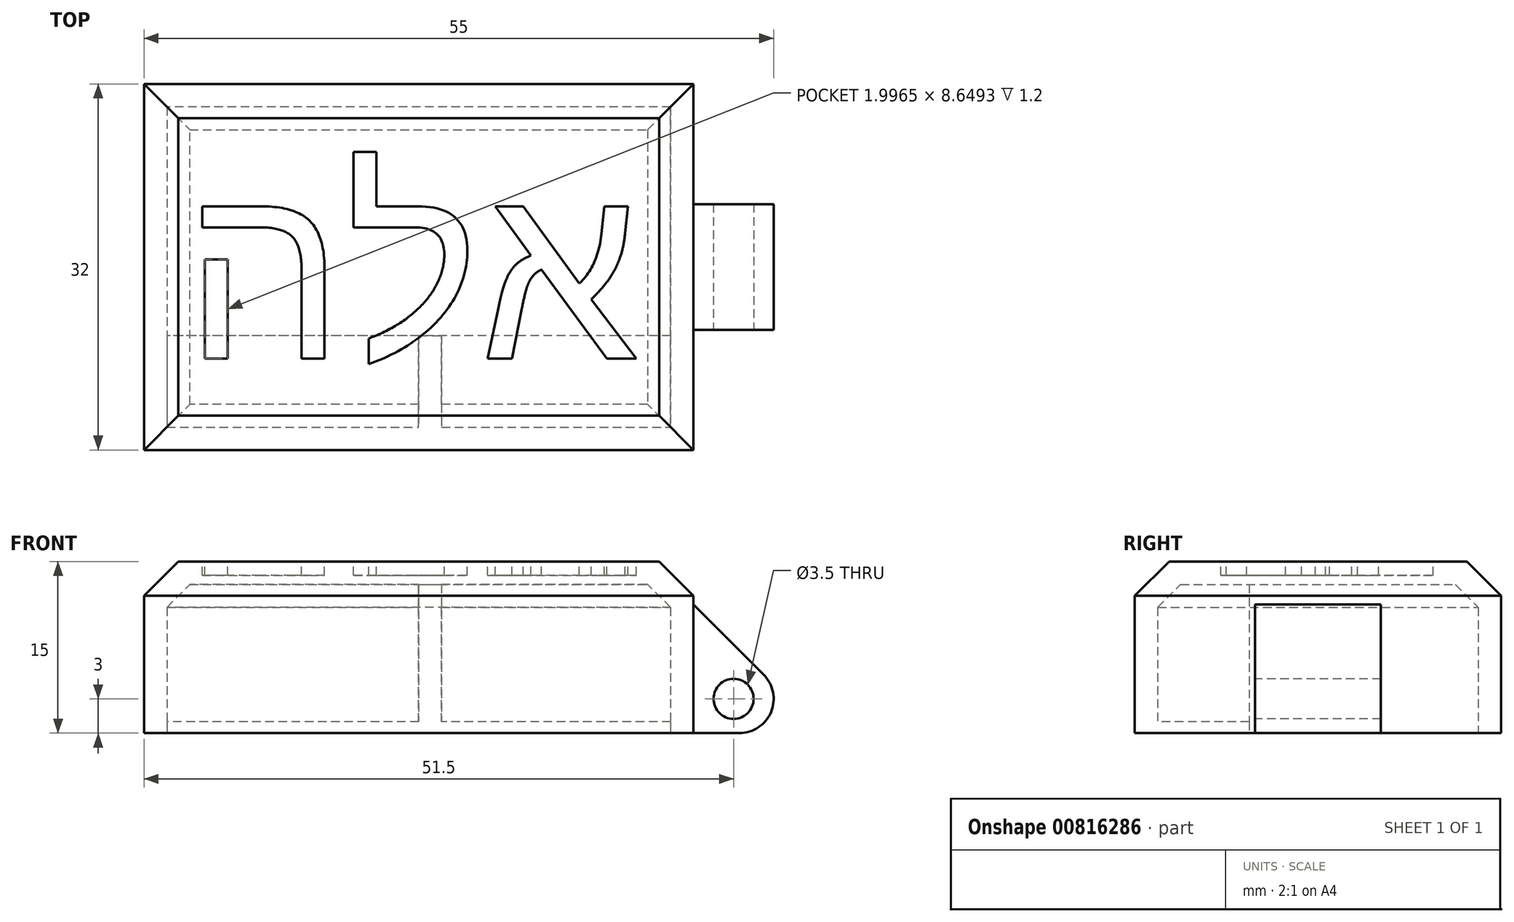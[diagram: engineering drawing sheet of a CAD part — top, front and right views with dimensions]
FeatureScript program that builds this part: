
annotation { "Feature Type Name" : "Feature", "Feature Type Description" : "" }
export const myFeature = defineFeature(function(context is Context, id is Id, definition is map)
    precondition{}
    {
        {
            var Q0;
            Q0=qCreatedBy(makeId("Top.planeOp"),FACE);
            var sketch = newSketch(context, id + "F0", { "sketchPlane" : qUnion([Q0])});
            skLineSegment(sketch, "E0.bottom", {"start": v(0, 0) * mm, "end": v(48, 0) * mm});
            skLineSegment(sketch, "E0.top", {"start": v(0, 32) * mm, "end": v(48, 32) * mm});
            skLineSegment(sketch, "E0.left", {"start": v(0, 0) * mm, "end": v(0, 32) * mm});
            skLineSegment(sketch, "E0.right", {"start": v(48, 0) * mm, "end": v(48, 32) * mm});
            skSolve(sketch);
        }
        {
            var Q0;
            Q0=makeQuery(id+"F0.imprint","IMPRINT",FACE,{"disambiguationData":[TD([[makeQuery(id+"F0.imprint","IMPRINT",EDGE,{"derivedFrom":sQuery(id+"F0.wireOp",EDGE,"E0.bottom")}),1.0]])]});
            extrude(context, id + "F1", {"entities" : qUnion([Q0]), "depth" : 15 * mm, "offsetDistance" : 25 * mm});
        }
        {
            var Q0;
            Q0=makeQuery(id+"F1.opExtrude","CAP_FACE",FACE,{"disambiguationData":[OSD([sQuery(id+"F0.wireOp",EDGE,"E0.bottom"),sQuery(id+"F0.wireOp",EDGE,"E0.top"),sQuery(id+"F0.wireOp",EDGE,"E0.left"),sQuery(id+"F0.wireOp",EDGE,"E0.right")])],"isStart":true});
            var sketch = newSketch(context, id + "F2", { "sketchPlane" : qUnion([Q0])});
            skLineSegment(sketch, "E1.bottom", {"start": v(46, -30) * mm, "end": v(2, -30) * mm});
            skLineSegment(sketch, "E1.top", {"start": v(46, -2) * mm, "end": v(2, -2) * mm});
            skLineSegment(sketch, "E1.left", {"start": v(46, -30) * mm, "end": v(46, -2) * mm});
            skLineSegment(sketch, "E1.right", {"start": v(2, -30) * mm, "end": v(2, -2) * mm});
            skSolve(sketch);
        }
        {
            var Q0;
            Q0=qSketchRegion(id+"F2",true);
            extrude(context, id + "F3", {"entities" : qUnion([Q0]), "operationType" : NewBodyOperationType.REMOVE, "oppositeDirection" : true, "depth" : 13 * mm, "offsetDistance" : 25 * mm});
        }
        {
            var Q0;
            Q0=makeQuery(id+"F1.opExtrude","CAP_FACE",FACE,{"disambiguationData":[OSD([sQuery(id+"F0.wireOp",EDGE,"E0.bottom"),sQuery(id+"F0.wireOp",EDGE,"E0.top"),sQuery(id+"F0.wireOp",EDGE,"E0.left"),sQuery(id+"F0.wireOp",EDGE,"E0.right")])],"isStart":true});
            var sketch = newSketch(context, id + "F4", { "sketchPlane" : qUnion([Q0])});
            skLineSegment(sketch, "E2.bottom", {"start": v(48, -10.5) * mm, "end": v(55, -10.5) * mm});
            skLineSegment(sketch, "E2.top", {"start": v(48, -21.5) * mm, "end": v(55, -21.5) * mm});
            skLineSegment(sketch, "E2.left", {"start": v(48, -10.5) * mm, "end": v(48, -21.5) * mm});
            skLineSegment(sketch, "E2.right", {"start": v(55, -10.5) * mm, "end": v(55, -21.5) * mm});
            skSolve(sketch);
        }
        {
            var Q0;
            Q0=makeQuery(id+"F4.imprint","IMPRINT",FACE,{"disambiguationData":[TD([[makeQuery(id+"F4.imprint","IMPRINT",EDGE,{"derivedFrom":sQuery(id+"F4.wireOp",EDGE,"E2.bottom")}),-1.0]])]});
            var Q1;
            Q1=makeQuery(id+"F4.imprint","IMPRINT",FACE,{"disambiguationData":[TD([[makeQuery(id+"F4.imprint","IMPRINT",EDGE,{"derivedFrom":sQuery(id+"F4.wireOp",EDGE,"Fs3PQJWO-v5HL-7R1I-baSF-Dp8QI7Y0G9z7.bottom")}),-1.0]])]});
            extrude(context, id + "F5", {"entities" : qUnion([Q0, Q1]), "operationType" : NewBodyOperationType.ADD, "oppositeDirection" : true, "depth" : 6 * mm, "offsetDistance" : 25 * mm});
        }
        {
            var Q0;
            Q0=makeQuery(id+"F5.opExtrude","SWEPT_FACE",FACE,{"disambiguationData":[OSD([sQuery(id+"F4.wireOp",EDGE,"E2.bottom")])]});
            var sketch = newSketch(context, id + "F6", { "sketchPlane" : qUnion([Q0])});
            skLineSegment(sketch, "E3", {"start": v(48, 6) * mm, "end": v(55, 0) * mm, "construction": true});
            skCircle(sketch, "E4", {"center": v(51.5, 3) * mm, "radius": 1.75 * mm});
            skSolve(sketch);
        }
        {
            var Q0;
            Q0=makeQuery(id+"F6.imprint","IMPRINT",FACE,{"disambiguationData":[TD([[makeQuery(id+"F6.imprint","IMPRINT",EDGE,{"derivedFrom":sQuery(id+"F6.wireOp",EDGE,"E4")}),1.0]])]});
            extrude(context, id + "F7", {"entities" : qUnion([Q0]), "operationType" : NewBodyOperationType.REMOVE, "oppositeDirection" : true, "depth" : 60.8 * mm, "offsetDistance" : 25 * mm});
        }
        {
            var Q0;
            Q0=makeQuery(id+"F5.opExtrude","CAP_EDGE",EDGE,{"disambiguationData":[OSD([sQuery(id+"F4.wireOp",EDGE,"E2.right")])],"isStart":true});
            var Q1;
            Q1=makeQuery(id+"F5.opExtrude","CAP_EDGE",EDGE,{"disambiguationData":[OSD([sQuery(id+"F4.wireOp",EDGE,"E2.right")])],"isStart":false});
            var Q2;
            Q2=makeQuery(id+"F5.opExtrude","CAP_EDGE",EDGE,{"disambiguationData":[OSD([sQuery(id+"F4.wireOp",EDGE,"Fs3PQJWO-v5HL-7R1I-baSF-Dp8QI7Y0G9z7.right")])],"isStart":false});
            var Q3;
            Q3=makeQuery(id+"F5.opExtrude","CAP_EDGE",EDGE,{"disambiguationData":[OSD([sQuery(id+"F4.wireOp",EDGE,"Fs3PQJWO-v5HL-7R1I-baSF-Dp8QI7Y0G9z7.right")])],"isStart":true});
            fillet(context, id + "F8", {"entities" : qUnion([Q0, Q1, Q2, Q3]), "tangentPropagation" : true, "radius" : 3 * mm, "defaultsChanged" : false, "vertexSettings" : [], "allowEdgeOverflow" : false});
        }
        {
            var Q0;
            Q0=makeQuery(id+"FWko5dZgeJsUJI3_1.boolean.opBoolean","MERGE",FACE,{"derivedFrom":[makeQuery(id+"F5.boolean.opBoolean","MERGE",FACE,{"derivedFrom":[makeQuery(id+"F1.opExtrude","CAP_FACE",FACE,{"disambiguationData":[OSD([sQuery(id+"F0.wireOp",EDGE,"E0.bottom"),sQuery(id+"F0.wireOp",EDGE,"E0.top"),sQuery(id+"F0.wireOp",EDGE,"E0.left"),sQuery(id+"F0.wireOp",EDGE,"E0.right")])],"isStart":true}),makeQuery(id+"F5.opExtrude","CAP_FACE",FACE,{"disambiguationData":[OSD([sQuery(id+"F4.wireOp",EDGE,"E2.bottom"),sQuery(id+"F4.wireOp",EDGE,"E2.top"),sQuery(id+"F4.wireOp",EDGE,"E2.left"),sQuery(id+"F4.wireOp",EDGE,"E2.right")])],"isStart":true}),makeQuery(id+"F5.opExtrude","CAP_FACE",FACE,{"disambiguationData":[OSD([sQuery(id+"F4.wireOp",EDGE,"Fs3PQJWO-v5HL-7R1I-baSF-Dp8QI7Y0G9z7.bottom"),sQuery(id+"F4.wireOp",EDGE,"Fs3PQJWO-v5HL-7R1I-baSF-Dp8QI7Y0G9z7.top"),sQuery(id+"F4.wireOp",EDGE,"Fs3PQJWO-v5HL-7R1I-baSF-Dp8QI7Y0G9z7.left"),sQuery(id+"F4.wireOp",EDGE,"Fs3PQJWO-v5HL-7R1I-baSF-Dp8QI7Y0G9z7.right")])],"isStart":true})]}),makeQuery(id+"FWko5dZgeJsUJI3_1.opExtrude","CAP_FACE",FACE,{"disambiguationData":[OSD([sQuery(id+"Fm630fHmEzdltA1_1.wireOp",EDGE,"m2h33AuZ-GarK-fSBx-g64L-yckGO1Rjv7rp.bottom"),sQuery(id+"Fm630fHmEzdltA1_1.wireOp",EDGE,"m2h33AuZ-GarK-fSBx-g64L-yckGO1Rjv7rp.top"),sQuery(id+"Fm630fHmEzdltA1_1.wireOp",EDGE,"m2h33AuZ-GarK-fSBx-g64L-yckGO1Rjv7rp.left"),sQuery(id+"Fm630fHmEzdltA1_1.wireOp",EDGE,"m2h33AuZ-GarK-fSBx-g64L-yckGO1Rjv7rp.right")])],"isStart":true})]});
            var sketch = newSketch(context, id + "F9", { "sketchPlane" : qUnion([Q0])});
            skLineSegment(sketch, "E5.bottom", {"start": v(46, -2) * mm, "end": v(2, -2) * mm});
            skLineSegment(sketch, "E5.top", {"start": v(46, -10) * mm, "end": v(2, -10) * mm});
            skLineSegment(sketch, "E5.left", {"start": v(46, -2) * mm, "end": v(46, -10) * mm});
            skLineSegment(sketch, "E5.right", {"start": v(2, -2) * mm, "end": v(2, -10) * mm});
            skSolve(sketch);
        }
        {
            var Q0;
            Q0=makeQuery(id+"F9.imprint","IMPRINT",FACE,{"disambiguationData":[TD([[makeQuery(id+"F9.imprint","IMPRINT",EDGE,{"derivedFrom":sQuery(id+"F9.wireOp",EDGE,"8anpZ1CY-tV0m-vv06-WH6s-fZvPGU5znIe8.bottom")}),1.0]])]});
            var Q1;
            Q1=makeQuery(id+"F9.imprint","IMPRINT",FACE,{"disambiguationData":[TD([[makeQuery(id+"F9.imprint","IMPRINT",EDGE,{"derivedFrom":sQuery(id+"F9.wireOp",EDGE,"E5.bottom")}),1.0]])]});
            extrude(context, id + "F10", {"entities" : qUnion([Q0, Q1]), "operationType" : NewBodyOperationType.ADD, "oppositeDirection" : true, "depth" : 1 * mm, "offsetDistance" : 25 * mm});
        }
        {
            var Q0;
            Q0=makeQuery(id+"F10.boolean.opBoolean","MERGE",FACE,{"derivedFrom":[makeQuery(id+"FWko5dZgeJsUJI3_1.boolean.opBoolean","MERGE",FACE,{"derivedFrom":[makeQuery(id+"F5.boolean.opBoolean","MERGE",FACE,{"derivedFrom":[makeQuery(id+"F1.opExtrude","CAP_FACE",FACE,{"disambiguationData":[OSD([sQuery(id+"F0.wireOp",EDGE,"E0.bottom"),sQuery(id+"F0.wireOp",EDGE,"E0.top"),sQuery(id+"F0.wireOp",EDGE,"E0.left"),sQuery(id+"F0.wireOp",EDGE,"E0.right")])],"isStart":true}),makeQuery(id+"F5.opExtrude","CAP_FACE",FACE,{"disambiguationData":[OSD([sQuery(id+"F4.wireOp",EDGE,"E2.bottom"),sQuery(id+"F4.wireOp",EDGE,"E2.top"),sQuery(id+"F4.wireOp",EDGE,"E2.left"),sQuery(id+"F4.wireOp",EDGE,"E2.right")])],"isStart":true}),makeQuery(id+"F5.opExtrude","CAP_FACE",FACE,{"disambiguationData":[OSD([sQuery(id+"F4.wireOp",EDGE,"Fs3PQJWO-v5HL-7R1I-baSF-Dp8QI7Y0G9z7.bottom"),sQuery(id+"F4.wireOp",EDGE,"Fs3PQJWO-v5HL-7R1I-baSF-Dp8QI7Y0G9z7.top"),sQuery(id+"F4.wireOp",EDGE,"Fs3PQJWO-v5HL-7R1I-baSF-Dp8QI7Y0G9z7.left"),sQuery(id+"F4.wireOp",EDGE,"Fs3PQJWO-v5HL-7R1I-baSF-Dp8QI7Y0G9z7.right")])],"isStart":true})]}),makeQuery(id+"FWko5dZgeJsUJI3_1.opExtrude","CAP_FACE",FACE,{"disambiguationData":[OSD([sQuery(id+"Fm630fHmEzdltA1_1.wireOp",EDGE,"m2h33AuZ-GarK-fSBx-g64L-yckGO1Rjv7rp.bottom"),sQuery(id+"Fm630fHmEzdltA1_1.wireOp",EDGE,"m2h33AuZ-GarK-fSBx-g64L-yckGO1Rjv7rp.top"),sQuery(id+"Fm630fHmEzdltA1_1.wireOp",EDGE,"m2h33AuZ-GarK-fSBx-g64L-yckGO1Rjv7rp.left"),sQuery(id+"Fm630fHmEzdltA1_1.wireOp",EDGE,"m2h33AuZ-GarK-fSBx-g64L-yckGO1Rjv7rp.right")])],"isStart":true})]}),makeQuery(id+"F10.opExtrude","CAP_FACE",FACE,{"disambiguationData":[OSD([sQuery(id+"F9.wireOp",EDGE,"8anpZ1CY-tV0m-vv06-WH6s-fZvPGU5znIe8.bottom"),sQuery(id+"F9.wireOp",EDGE,"8anpZ1CY-tV0m-vv06-WH6s-fZvPGU5znIe8.top"),sQuery(id+"F9.wireOp",EDGE,"8anpZ1CY-tV0m-vv06-WH6s-fZvPGU5znIe8.left"),sQuery(id+"F9.wireOp",EDGE,"8anpZ1CY-tV0m-vv06-WH6s-fZvPGU5znIe8.right")])],"isStart":true}),makeQuery(id+"F10.opExtrude","CAP_FACE",FACE,{"disambiguationData":[OSD([sQuery(id+"F9.wireOp",EDGE,"E5.bottom"),sQuery(id+"F9.wireOp",EDGE,"E5.top"),sQuery(id+"F9.wireOp",EDGE,"E5.left"),sQuery(id+"F9.wireOp",EDGE,"E5.right")])],"isStart":true})]});
            var sketch = newSketch(context, id + "F11", { "sketchPlane" : qUnion([Q0])});
            skLineSegment(sketch, "E6.bottom", {"start": v(24, -10) * mm, "end": v(26, -10) * mm});
            skLineSegment(sketch, "E6.top", {"start": v(24, 0) * mm, "end": v(26, 0) * mm});
            skLineSegment(sketch, "E6.left", {"start": v(24, -10) * mm, "end": v(24, 0) * mm});
            skLineSegment(sketch, "E6.right", {"start": v(26, -10) * mm, "end": v(26, 0) * mm});
            skSolve(sketch);
        }
        {
            var Q0;
            Q0=makeQuery(id+"F11.imprint","IMPRINT",FACE,{"disambiguationData":[TD([[makeQuery(id+"F11.imprint","IMPRINT",EDGE,{"derivedFrom":sQuery(id+"F11.wireOp",EDGE,"16yneMW3-uMlb-iSc8-jPiz-rwLQxktEgYX5.bottom")}),-1.0]])]});
            var Q1;
            Q1=makeQuery(id+"F11.imprint","IMPRINT",FACE,{"disambiguationData":[TD([[makeQuery(id+"F11.imprint","IMPRINT",EDGE,{"derivedFrom":sQuery(id+"F11.wireOp",EDGE,"E6.bottom")}),-1.0]])]});
            var Q2;
            {var subQ0=sQuery(id+"F2.wireOp",EDGE,"E1.bottom");var subQ1=sQuery(id+"F2.wireOp",EDGE,"E1.left");var subQ2=sQuery(id+"F2.wireOp",EDGE,"E1.right");Q2=makeQuery(id+"FWko5dZgeJsUJI3_1.boolean.opBoolean","SPLIT",FACE,{"disambiguationData":[TD([makeQuery(id+"F3.boolean.opBoolean","COPY",FACE,{"derivedFrom":makeQuery(id+"F3.opExtrude","SWEPT_FACE",FACE,{"disambiguationData":[OSD([subQ0])]})})])],"derivedFrom":makeQuery(id+"F3.boolean.opBoolean","COPY",FACE,{"derivedFrom":makeQuery(id+"F3.opExtrude","CAP_FACE",FACE,{"disambiguationData":[OSD([subQ0,sQuery(id+"F2.wireOp",EDGE,"E1.top"),subQ1,subQ2])],"isStart":false})})});}
            extrude(context, id + "F12", {"entities" : qUnion([Q0, Q1]), "operationType" : NewBodyOperationType.ADD, "endBound" : BoundingType.UP_TO_SURFACE, "oppositeDirection" : true, "depth" : 25 * mm, "endBoundEntityFace" : qUnion([Q2]), "offsetDistance" : 25 * mm});
        }
        {
            var Q0;
            Q0=makeQuery(id+"F1.opExtrude","CAP_EDGE",EDGE,{"disambiguationData":[OSD([sQuery(id+"F0.wireOp",EDGE,"E0.right")])],"isStart":false});
            var Q1;
            Q1=makeQuery(id+"F1.opExtrude","CAP_EDGE",EDGE,{"disambiguationData":[OSD([sQuery(id+"F0.wireOp",EDGE,"E0.bottom")])],"isStart":false});
            var Q2;
            Q2=makeQuery(id+"F1.opExtrude","CAP_EDGE",EDGE,{"disambiguationData":[OSD([sQuery(id+"F0.wireOp",EDGE,"E0.left")])],"isStart":false});
            var Q3;
            Q3=makeQuery(id+"F1.opExtrude","CAP_EDGE",EDGE,{"disambiguationData":[OSD([sQuery(id+"F0.wireOp",EDGE,"E0.top")])],"isStart":false});
            chamfer(context, id + "F13", {"entities" : qUnion([Q0, Q1, Q2, Q3]), "width" : 3 * mm, "tangentPropagation" : true});
        }
        {
            var Q0;
            Q0=makeQuery(id+"F3.boolean.opBoolean","COPY",EDGE,{"derivedFrom":makeQuery(id+"F3.opExtrude","CAP_EDGE",EDGE,{"disambiguationData":[OSD([sQuery(id+"F2.wireOp",EDGE,"E1.bottom")])],"isStart":false})});
            var Q1;
            Q1=makeQuery(id+"F3.boolean.opBoolean","COPY",EDGE,{"derivedFrom":makeQuery(id+"F3.opExtrude","CAP_EDGE",EDGE,{"disambiguationData":[OSD([sQuery(id+"F2.wireOp",EDGE,"E1.left")])],"isStart":false})});
            var Q2;
            Q2=makeQuery(id+"F3.boolean.opBoolean","COPY",EDGE,{"derivedFrom":makeQuery(id+"F3.opExtrude","CAP_EDGE",EDGE,{"disambiguationData":[OSD([sQuery(id+"F2.wireOp",EDGE,"E1.top")])],"isStart":false})});
            var Q3;
            Q3=makeQuery(id+"F3.boolean.opBoolean","COPY",EDGE,{"derivedFrom":makeQuery(id+"F3.opExtrude","CAP_EDGE",EDGE,{"disambiguationData":[OSD([sQuery(id+"F2.wireOp",EDGE,"E1.right")])],"isStart":false})});
            var Q4;
            Q4=makeQuery(id+"FWko5dZgeJsUJI3_1.opExtrude","CAP_EDGE",EDGE,{"disambiguationData":[OSD([sQuery(id+"Fm630fHmEzdltA1_1.wireOp",EDGE,"m2h33AuZ-GarK-fSBx-g64L-yckGO1Rjv7rp.top")])],"isStart":false});
            var Q5;
            Q5=makeQuery(id+"FWko5dZgeJsUJI3_1.opExtrude","CAP_EDGE",EDGE,{"disambiguationData":[OSD([sQuery(id+"Fm630fHmEzdltA1_1.wireOp",EDGE,"m2h33AuZ-GarK-fSBx-g64L-yckGO1Rjv7rp.bottom")])],"isStart":false});
            chamfer(context, id + "F14", {"entities" : qUnion([Q0, Q1, Q2, Q3, Q4, Q5]), "width" : 2 * mm, "tangentPropagation" : true});
        }
        {
            var Q0;
            Q0=makeQuery(id+"F5.opExtrude","SWEPT_FACE",FACE,{"disambiguationData":[OSD([sQuery(id+"F4.wireOp",EDGE,"E2.bottom")])]});
            var sketch = newSketch(context, id + "F15", { "sketchPlane" : qUnion([Q0])});
            skLineSegment(sketch, "E7", {"start": v(48, 6) * mm, "end": v(48, 11.24) * mm});
            skLineSegment(sketch, "E8", {"start": v(48, 11.24) * mm, "end": v(54.12, 5.12) * mm});
            skArc(sketch, "E9.0", {"start": v(54.12, 5.12) * mm, "mid": v(53.15, 5.77) * mm, "end": v(52, 6) * mm});
            skLineSegment(sketch, "E9.1", {"start": v(48, 6) * mm, "end": v(52, 6) * mm});
            skPoint(sketch, "E10.orphan", {"position": v(52, 0) * mm});
            skSolve(sketch);
        }
        {
            var Q0;
            Q0=makeQuery(id+"F15.imprint","IMPRINT",FACE,{"disambiguationData":[TD([[makeQuery(id+"F15.imprint","IMPRINT",EDGE,{"derivedFrom":sQuery(id+"F15.wireOp",EDGE,"E7")}),-1.0]])]});
            var Q1;
            Q1=makeQuery(id+"F5.opExtrude","SWEPT_FACE",FACE,{"disambiguationData":[OSD([sQuery(id+"F4.wireOp",EDGE,"E2.top")])]});
            extrude(context, id + "F16", {"entities" : qUnion([Q0]), "operationType" : NewBodyOperationType.ADD, "endBound" : BoundingType.UP_TO_SURFACE, "oppositeDirection" : true, "depth" : 25 * mm, "endBoundEntityFace" : qUnion([Q1]), "offsetDistance" : 25 * mm});
        }
        {
            var Q0;
            Q0=makeQuery(id+"F1.opExtrude","CAP_FACE",FACE,{"disambiguationData":[OSD([sQuery(id+"F0.wireOp",EDGE,"E0.bottom"),sQuery(id+"F0.wireOp",EDGE,"E0.top"),sQuery(id+"F0.wireOp",EDGE,"E0.left"),sQuery(id+"F0.wireOp",EDGE,"E0.right")])],"isStart":false});
            var sketch = newSketch(context, id + "F17", { "sketchPlane" : qUnion([Q0])});
            skText(sketch, "E11", { "text": "הלא", "fontName": "Arimo-Regular.ttf"});
            skLineSegment(sketch, "E12", {"start": v(3, 16) * mm, "end": v(3.46, 16) * mm, "construction": true});
            skLineSegment(sketch, "E13", {"start": v(24, 3) * mm, "end": v(24, 8) * mm, "construction": true});
            skLineSegment(sketch, "E14", {"start": v(24, 24) * mm, "end": v(24, 29) * mm, "construction": true});
            skLineSegment(sketch, "E15", {"start": v(44.54, 16) * mm, "end": v(45, 16) * mm, "construction": true});
            const initialGuessF17  = {"E11": [0.00346, 0.008, 1, 0, 0.016]};
            skSetInitialGuess(sketch, initialGuessF17);
            skSolve(sketch);
        }
        {
            var Q0;
            Q0 = qSketchRegion(id + "F17", true);
            extrude(context, id + "F18", {"entities" : qUnion([Q0]), "operationType" : NewBodyOperationType.REMOVE, "oppositeDirection" : true, "depth" : 1.2 * mm, "offsetDistance" : 25 * mm});
        }
    });
